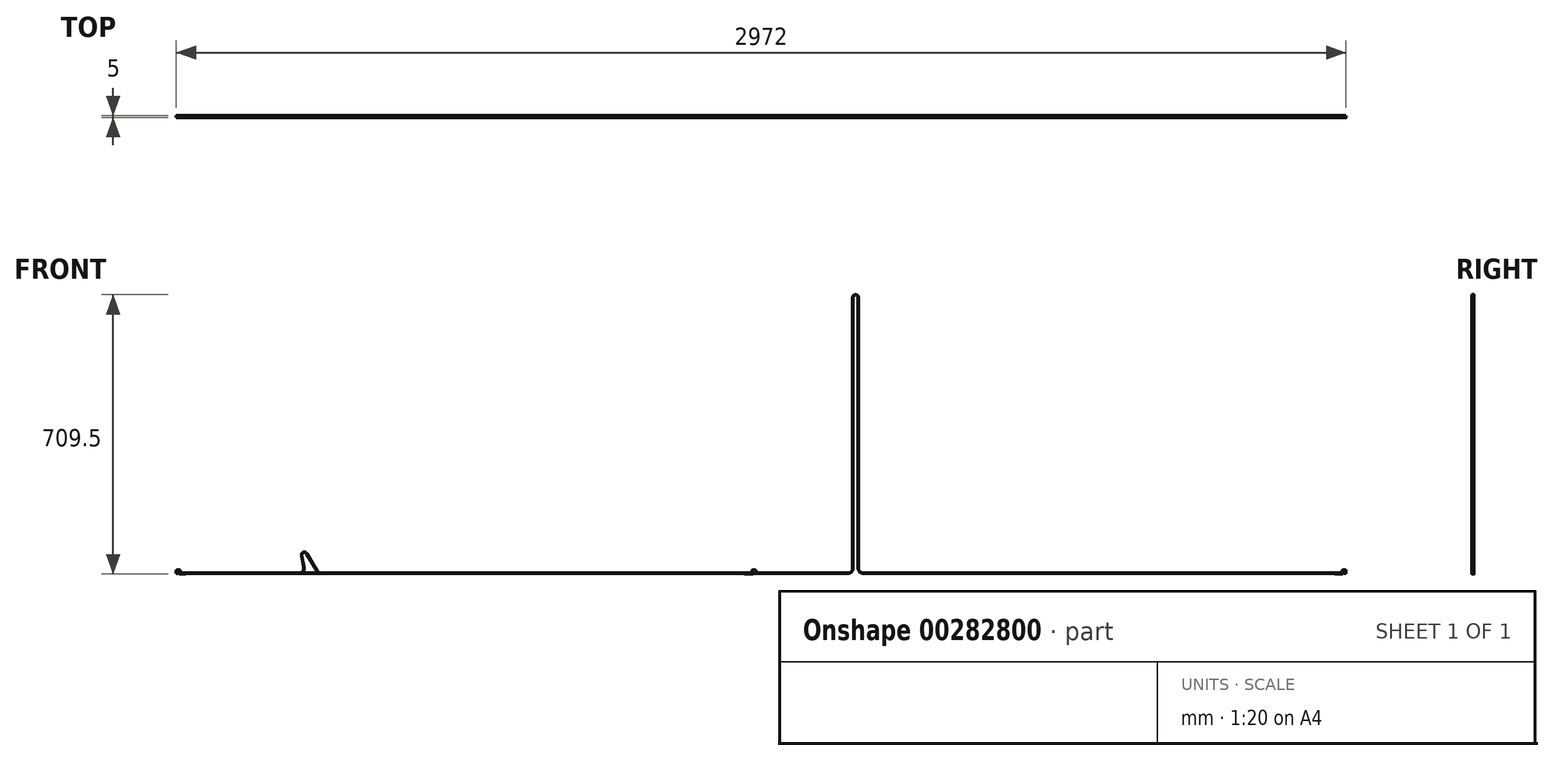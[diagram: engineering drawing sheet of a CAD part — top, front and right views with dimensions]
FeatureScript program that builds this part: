
annotation { "Feature Type Name" : "Feature", "Feature Type Description" : "" }
export const myFeature = defineFeature(function(context is Context, id is Id, definition is map)
    precondition{}
    {
        {
            var Q0;
            Q0=qCreatedBy(makeId("Front.planeOp"),FACE);
            var sketch = newSketch(context, id + "F0", { "sketchPlane" : qUnion([Q0])});
            skArc(sketch, "E0", {"start": v(1721, 0) * mm, "mid": v(1729.49, 3.51) * mm, "end": v(1733, 12) * mm});
            skLineSegment(sketch, "E1", {"start": v(1733, 12) * mm, "end": v(1733, 700) * mm});
            skArc(sketch, "E2", {"start": v(1747, 700) * mm, "mid": v(1740, 707) * mm, "end": v(1733, 700) * mm});
            skLineSegment(sketch, "E3", {"start": v(1747, 700) * mm, "end": v(1747, 12) * mm});
            skArc(sketch, "E4", {"start": v(1747, 12) * mm, "mid": v(1750.51, 3.51) * mm, "end": v(1759, 0) * mm});
            skLineSegment(sketch, "E5", {"start": v(1759, 0) * mm, "end": v(2975.5, 0) * mm});
            skLineSegment(sketch, "E6.bottom", {"start": v(0, 0) * mm, "end": v(27.5, 0) * mm, "construction": true});
            skLineSegment(sketch, "E6.top", {"start": v(0, 5) * mm, "end": v(27.5, 5) * mm, "construction": true});
            skLineSegment(sketch, "E6.left", {"start": v(0, 0) * mm, "end": v(0, 5) * mm, "construction": true});
            skLineSegment(sketch, "E6.right", {"start": v(27.5, 0) * mm, "end": v(27.5, 5) * mm, "construction": true});
            skLineSegment(sketch, "E7", {"start": v(13, 5) * mm, "end": v(13, 0) * mm, "construction": true});
            skLineSegment(sketch, "E8", {"start": v(19, 5) * mm, "end": v(19, 0) * mm, "construction": true});
            skLineSegment(sketch, "E9", {"start": v(15, 5) * mm, "end": v(15, 0) * mm, "construction": true});
            skLineSegment(sketch, "E10", {"start": v(17, 5) * mm, "end": v(17, 0) * mm, "construction": true});
            skLineSegment(sketch, "E11", {"start": v(21, 5) * mm, "end": v(21, 0) * mm, "construction": true});
            skLineSegment(sketch, "E12", {"start": v(24, 5) * mm, "end": v(24, 0) * mm, "construction": true});
            skLineSegment(sketch, "E13", {"start": v(1721, 0) * mm, "end": v(24.5, 0) * mm});
            skLineSegment(sketch, "E14", {"start": v(23.5, 1) * mm, "end": v(23.5, 6.25) * mm});
            skLineSegment(sketch, "E15", {"start": v(22.5, 7.25) * mm, "end": v(15.5, 7.25) * mm});
            skLineSegment(sketch, "E16", {"start": v(14.5, 6.25) * mm, "end": v(14.5, 0.75) * mm});
            skLineSegment(sketch, "E17", {"start": v(15.5, -0.25) * mm, "end": v(17.5, -0.25) * mm});
            skLineSegment(sketch, "E18", {"start": v(18.5, 0.75) * mm, "end": v(18.5, 5) * mm});
            skLineSegment(sketch, "E19", {"start": v(19.5, 6) * mm, "end": v(21, 6) * mm});
            skLineSegment(sketch, "E20", {"start": v(22, 5) * mm, "end": v(22, -0.5) * mm});
            skLineSegment(sketch, "E21", {"start": v(23, -1.5) * mm, "end": v(37.41, -1.5) * mm});
            skPoint(sketch, "E22.visualSharp", {"position": v(14.5, 7.25) * mm});
            skArc(sketch, "E22.filletArc", {"start": v(15.5, 7.25) * mm, "mid": v(14.8, 6.96) * mm, "end": v(14.5, 6.25) * mm});
            skPoint(sketch, "E23.visualSharp", {"position": v(14.5, -0.25) * mm});
            skArc(sketch, "E23.filletArc", {"start": v(14.5, 0.75) * mm, "mid": v(14.8, 0.04) * mm, "end": v(15.5, -0.25) * mm});
            skPoint(sketch, "E24.visualSharp", {"position": v(18.5, -0.25) * mm});
            skArc(sketch, "E24.filletArc", {"start": v(17.5, -0.25) * mm, "mid": v(18.2, 0.04) * mm, "end": v(18.5, 0.75) * mm});
            skPoint(sketch, "E25.visualSharp", {"position": v(18.5, 6) * mm});
            skArc(sketch, "E25.filletArc", {"start": v(19.5, 6) * mm, "mid": v(18.8, 5.7) * mm, "end": v(18.5, 5) * mm});
            skPoint(sketch, "E26.visualSharp", {"position": v(22, 6) * mm});
            skArc(sketch, "E26.filletArc", {"start": v(22, 5) * mm, "mid": v(21.7, 5.7) * mm, "end": v(21, 6) * mm});
            skPoint(sketch, "E27.visualSharp", {"position": v(22, -1.5) * mm});
            skArc(sketch, "E27.filletArc", {"start": v(22, -0.5) * mm, "mid": v(22.3, -1.2) * mm, "end": v(23, -1.5) * mm});
            skPoint(sketch, "E28.visualSharp", {"position": v(23.5, 0) * mm});
            skArc(sketch, "E28.filletArc", {"start": v(23.5, 1) * mm, "mid": v(23.8, 0.3) * mm, "end": v(24.5, 0) * mm});
            skPoint(sketch, "E29.visualSharp", {"position": v(23.5, 7.25) * mm});
            skArc(sketch, "E29.filletArc", {"start": v(23.5, 6.25) * mm, "mid": v(23.2, 6.96) * mm, "end": v(22.5, 7.25) * mm});
            skArc(sketch, "E30.MirrorCS", {"start": v(2978, 5) * mm, "mid": v(2978.3, 5.7) * mm, "end": v(2979, 6) * mm});
            skArc(sketch, "E31.MirrorCS", {"start": v(2976.5, 1) * mm, "mid": v(2976.2, 0.3) * mm, "end": v(2975.5, 0) * mm});
            skLineSegment(sketch, "E32.MirrorCS", {"start": v(2977, -1.5) * mm, "end": v(2957, -1.5) * mm});
            skLineSegment(sketch, "E33.MirrorCS", {"start": v(2985.5, 6.25) * mm, "end": v(2985.5, 0.75) * mm});
            skArc(sketch, "E34.MirrorCS", {"start": v(2976.5, 6.25) * mm, "mid": v(2976.8, 6.96) * mm, "end": v(2977.5, 7.25) * mm});
            skArc(sketch, "E35.MirrorCS", {"start": v(2980.5, 6) * mm, "mid": v(2981.2, 5.7) * mm, "end": v(2981.5, 5) * mm});
            skLineSegment(sketch, "E36.MirrorCS", {"start": v(2981.5, 0.75) * mm, "end": v(2981.5, 5) * mm});
            skArc(sketch, "E37.MirrorCS", {"start": v(2984.5, 7.25) * mm, "mid": v(2985.2, 6.96) * mm, "end": v(2985.5, 6.25) * mm});
            skArc(sketch, "E38.MirrorCS", {"start": v(2978, -0.5) * mm, "mid": v(2977.7, -1.2) * mm, "end": v(2977, -1.5) * mm});
            skLineSegment(sketch, "E39.MirrorCS", {"start": v(2977.5, 7.25) * mm, "end": v(2984.5, 7.25) * mm});
            skArc(sketch, "E40.MirrorCS", {"start": v(2985.5, 0.75) * mm, "mid": v(2985.2, 0.04) * mm, "end": v(2984.5, -0.25) * mm});
            skArc(sketch, "E41.MirrorCS", {"start": v(2982.5, -0.25) * mm, "mid": v(2981.8, 0.04) * mm, "end": v(2981.5, 0.75) * mm});
            skLineSegment(sketch, "E42.MirrorCS", {"start": v(2984.5, -0.25) * mm, "end": v(2982.5, -0.25) * mm});
            skLineSegment(sketch, "E43.MirrorCS", {"start": v(2978, 5) * mm, "end": v(2978, -0.5) * mm});
            skLineSegment(sketch, "E44.MirrorCS", {"start": v(2976.5, 1) * mm, "end": v(2976.5, 6.25) * mm});
            skLineSegment(sketch, "E45.MirrorCS", {"start": v(2980.5, 6) * mm, "end": v(2979, 6) * mm});
            skSolve(sketch);
        }
        {
            var Q0;
            Q0=qCreatedBy(makeId("Right.planeOp"),FACE);
            var Q1;
            Q1=sQuery(id+"F0.wireOp",VERTEX,"E21.end");
            cPlane(context, id + "F1", {"entities" : qUnion([Q0, Q1]), "cplaneType" : CPlaneType.PLANE_POINT, "offset" : 50 * mm, "width" : 150 * mm, "height" : 150 * mm});
        }
        {
            var Q0;
            Q0=qCreatedBy(id+"F1.planeOp",FACE);
            var sketch = newSketch(context, id + "F2", { "sketchPlane" : qUnion([Q0])});
            skLineSegment(sketch, "E46.bottom", {"start": v(2.5, -1) * mm, "end": v(-2.5, -1) * mm});
            skLineSegment(sketch, "E46.top", {"start": v(2.5, -2) * mm, "end": v(-2.5, -2) * mm});
            skLineSegment(sketch, "E46.left", {"start": v(2.5, -2) * mm, "end": v(2.5, -1) * mm});
            skLineSegment(sketch, "E46.right", {"start": v(-2.5, -2) * mm, "end": v(-2.5, -1) * mm});
            skLineSegment(sketch, "E47", {"start": v(2.5, -1.5) * mm, "end": v(-2.5, -1.5) * mm, "construction": true});
            skSolve(sketch);
        }
        {
            var Q0;
            Q0=qSketchRegion(id+"F2",true);
            var Q1;
            Q1=qConstructionFilter(qBodyType(qCreatedBy(id+"F0",EDGE),BodyType.WIRE),ConstructionObject.NO);
            sweep(context, id + "F3", {"profiles" : qUnion([Q0]), "path" : qUnion([Q1])});
        }
        {
            var Q0;
            Q0=qCreatedBy(makeId("Front.planeOp"),FACE);
            var sketch = newSketch(context, id + "F4", { "sketchPlane" : qUnion([Q0])});
            skLineSegment(sketch, "E48", {"start": v(24.5, 0) * mm, "end": v(326.5, 0) * mm});
            skLineSegment(sketch, "E49", {"start": v(338.3, 14.2) * mm, "end": v(332.62, 44.72) * mm});
            skLineSegment(sketch, "E50", {"start": v(345.49, 49.62) * mm, "end": v(372, 5.8) * mm});
            skLineSegment(sketch, "E51", {"start": v(382.27, 0) * mm, "end": v(1476.27, 0) * mm});
            skPoint(sketch, "E52.visualSharp", {"position": v(340.94, 0) * mm});
            skArc(sketch, "E52.filletArc", {"start": v(326.5, 0) * mm, "mid": v(335.73, 4.33) * mm, "end": v(338.3, 14.2) * mm});
            skPoint(sketch, "E53.visualSharp", {"position": v(375.5, 0) * mm});
            skArc(sketch, "E53.filletArc", {"start": v(372, 5.8) * mm, "mid": v(376.37, 1.55) * mm, "end": v(382.27, 0) * mm});
            skArc(sketch, "E54", {"start": v(345.49, 49.62) * mm, "mid": v(337, 52.54) * mm, "end": v(332.62, 44.72) * mm});
            skArc(sketch, "E55", {"start": v(23.5, 1) * mm, "mid": v(23.8, 0.3) * mm, "end": v(24.5, 0) * mm});
            skLineSegment(sketch, "E56", {"start": v(23.5, 1) * mm, "end": v(23.5, 6.25) * mm});
            skArc(sketch, "E57", {"start": v(23.5, 6.25) * mm, "mid": v(23.2, 6.96) * mm, "end": v(22.5, 7.25) * mm});
            skLineSegment(sketch, "E58", {"start": v(22.5, 7.25) * mm, "end": v(15.5, 7.25) * mm});
            skArc(sketch, "E59", {"start": v(15.5, 7.25) * mm, "mid": v(14.8, 6.96) * mm, "end": v(14.5, 6.25) * mm});
            skLineSegment(sketch, "E60", {"start": v(14.5, 6.25) * mm, "end": v(14.5, 0.75) * mm});
            skArc(sketch, "E61", {"start": v(14.5, 0.75) * mm, "mid": v(14.8, 0.04) * mm, "end": v(15.5, -0.25) * mm});
            skLineSegment(sketch, "E62", {"start": v(15.5, -0.25) * mm, "end": v(17.5, -0.25) * mm});
            skLineSegment(sketch, "E63", {"start": v(18.5, 0.75) * mm, "end": v(18.5, 5) * mm});
            skLineSegment(sketch, "E64", {"start": v(19.5, 6) * mm, "end": v(21, 6) * mm});
            skLineSegment(sketch, "E65", {"start": v(22, 5) * mm, "end": v(22, -0.5) * mm});
            skLineSegment(sketch, "E66", {"start": v(23, -1.5) * mm, "end": v(37.41, -1.5) * mm});
            skArc(sketch, "E67", {"start": v(17.5, -0.25) * mm, "mid": v(18.2, 0.04) * mm, "end": v(18.5, 0.75) * mm});
            skArc(sketch, "E68", {"start": v(19.5, 6) * mm, "mid": v(18.8, 5.7) * mm, "end": v(18.5, 5) * mm});
            skArc(sketch, "E69", {"start": v(22, 5) * mm, "mid": v(21.7, 5.7) * mm, "end": v(21, 6) * mm});
            skArc(sketch, "E70", {"start": v(22, -0.5) * mm, "mid": v(22.3, -1.2) * mm, "end": v(23, -1.5) * mm});
            skArc(sketch, "E71.MirrorCS", {"start": v(1485.27, 7.25) * mm, "mid": v(1485.97, 6.96) * mm, "end": v(1486.27, 6.25) * mm});
            skLineSegment(sketch, "E72.MirrorCS", {"start": v(1481.27, 6) * mm, "end": v(1479.77, 6) * mm});
            skArc(sketch, "E73.MirrorCS", {"start": v(1481.27, 6) * mm, "mid": v(1481.97, 5.7) * mm, "end": v(1482.27, 5) * mm});
            skArc(sketch, "E74.MirrorCS", {"start": v(1486.27, 0.75) * mm, "mid": v(1485.97, 0.04) * mm, "end": v(1485.27, -0.25) * mm});
            skArc(sketch, "E75.MirrorCS", {"start": v(1477.27, 6.25) * mm, "mid": v(1477.56, 6.96) * mm, "end": v(1478.27, 7.25) * mm});
            skArc(sketch, "E76.MirrorCS", {"start": v(1478.77, -0.5) * mm, "mid": v(1478.47, -1.2) * mm, "end": v(1477.77, -1.5) * mm});
            skArc(sketch, "E77.MirrorCS", {"start": v(1483.27, -0.25) * mm, "mid": v(1482.56, 0.04) * mm, "end": v(1482.27, 0.75) * mm});
            skArc(sketch, "E78.MirrorCS", {"start": v(1478.77, 5) * mm, "mid": v(1479.06, 5.7) * mm, "end": v(1479.77, 6) * mm});
            skLineSegment(sketch, "E79.MirrorCS", {"start": v(1485.27, -0.25) * mm, "end": v(1483.27, -0.25) * mm});
            skArc(sketch, "E80.MirrorCS", {"start": v(1477.27, 1) * mm, "mid": v(1476.97, 0.3) * mm, "end": v(1476.27, 0) * mm});
            skLineSegment(sketch, "E81.MirrorCS", {"start": v(1477.27, 1) * mm, "end": v(1477.27, 6.25) * mm});
            skLineSegment(sketch, "E82.MirrorCS", {"start": v(1477.77, -1.5) * mm, "end": v(1457.77, -1.5) * mm});
            skLineSegment(sketch, "E83.MirrorCS", {"start": v(1478.27, 7.25) * mm, "end": v(1485.27, 7.25) * mm});
            skLineSegment(sketch, "E84.MirrorCS", {"start": v(1478.77, 5) * mm, "end": v(1478.77, -0.5) * mm});
            skLineSegment(sketch, "E85.MirrorCS", {"start": v(1482.27, 0.75) * mm, "end": v(1482.27, 5) * mm});
            skLineSegment(sketch, "E86.MirrorCS", {"start": v(1486.27, 6.25) * mm, "end": v(1486.27, 0.75) * mm});
            skSolve(sketch);
        }
        {
            var Q0;
            Q0=qSketchRegion(id+"F2",true);
            var Q1;
            Q1=qConstructionFilter(qBodyType(qCreatedBy(id+"F4",EDGE),BodyType.WIRE),ConstructionObject.NO);
            sweep(context, id + "F5", {"profiles" : qUnion([Q0]), "path" : qUnion([Q1])});
        }
    });
